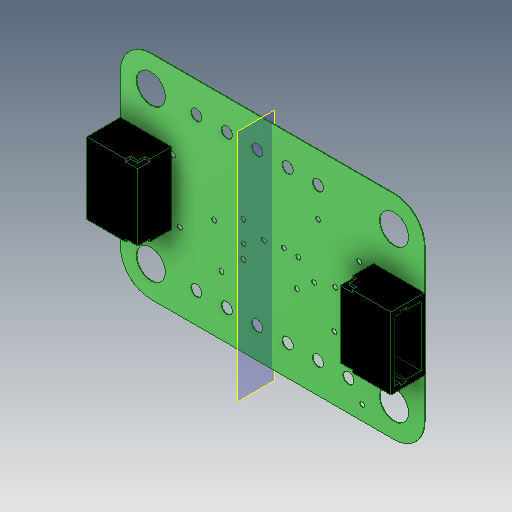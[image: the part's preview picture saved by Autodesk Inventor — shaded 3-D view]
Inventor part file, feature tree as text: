
AUTODESK INVENTOR PART (.ipt)
format: ipt  version: 2020 (Build 240168000, 168)  size: 264,192 bytes
history: native  units: in
note: dims shown in document units (in); Inventor stores cm internally (conversion verified against a paired STEP export)
features: extrude x3, sketch x3, plane x2, mirror x2
ambient origin geometry x8: Origin, YZ Plane, XZ Plane, XY Plane, X Axis, Y Axis, Z Axis, Center Point
bodies: Solid1 (feature_tree), Body1 (feature_tree)
feature tree (10):
  extrude  "Extrusion1"  Depth=0.1102in
  extrude  "Extrusion2"  Depth=0.1969in
  extrude  "Extrusion3"  Depth=0.2126in
  plane  "Work Plane1"
  mirror  "Mirror1"
  plane  "Work Plane2"
  mirror  "Mirror2"
  sketch  "Sketch1"  dims[d0=0.2362in d1=0.1102in]
  sketch  "Sketch2"  dims[d2=0.1673in d3=0.0in d4=0.1969in]
  sketch  "Sketch3"  dims[d5=0.0882in d6=0.2126in d7=0.0197in d8=0.0197in d9=0.1575in d10=0.0in d11=0.0394in d12=0.0394in d13=0.0157in d14=0.0157in d15=0.0079in d16=0.0in d17=0.0197in d18=1.9685in d19=0.0197in d20=1.9685in]
